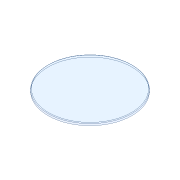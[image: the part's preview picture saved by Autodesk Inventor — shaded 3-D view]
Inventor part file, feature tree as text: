
AUTODESK INVENTOR PART (.ipt)
format: ipt  version: 2020.3 (Build 243373000, 373)  size: 86,016 bytes
history: native  units: mm
features: extrude x1, fillet x1, sketch x1
ambient origin geometry x8: Origin, YZ Plane, XZ Plane, XY Plane, X Axis, Y Axis, Z Axis, Center Point
bodies: Solid1 (feature_tree)
feature tree (3):
  extrude  "Extrusion1"  Depth=2.0mm TaperAngle=0.0deg
  fillet  "Fillet1"  Radius=0.5mm
  sketch  "Sketch1"  dims[d0=70.0mm d1=2.0mm d2=0.0mm d3=0.5mm]
